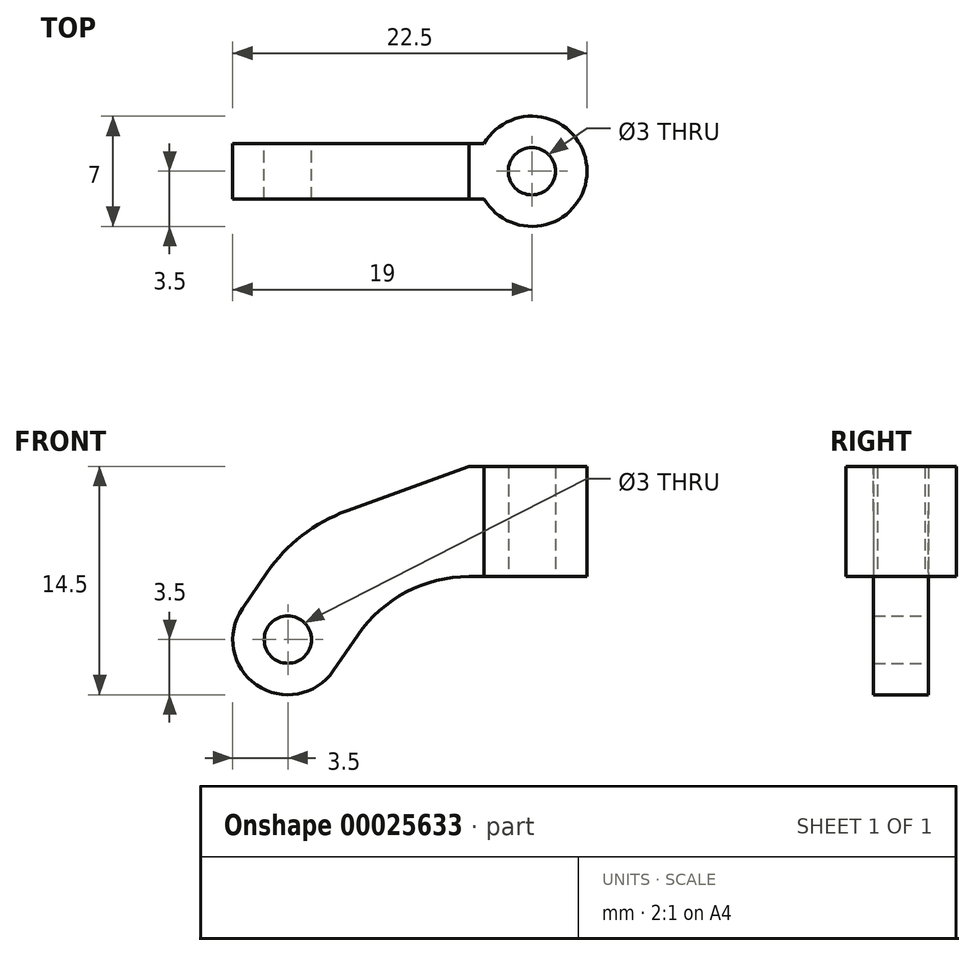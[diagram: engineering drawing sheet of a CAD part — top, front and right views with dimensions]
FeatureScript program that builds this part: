
annotation { "Feature Type Name" : "Feature", "Feature Type Description" : "" }
export const myFeature = defineFeature(function(context is Context, id is Id, definition is map)
    precondition{}
    {
        {
            var Q0;
            Q0=qCreatedBy(makeId("Top.planeOp"),FACE);
            var sketch = newSketch(context, id + "F0", { "sketchPlane" : qUnion([Q0])});
            skCircle(sketch, "E0", {"center": v(0, 0) * mm, "radius": 1.5 * mm});
            skCircle(sketch, "E1", {"center": v(0, 0) * mm, "radius": 3.5 * mm});
            skSolve(sketch);
        }
        {
            var Q0;
            Q0=makeQuery(id+"F0.imprint","IMPRINT",FACE,{"disambiguationData":[TD([[makeQuery(id+"F0.imprint","IMPRINT",EDGE,{"derivedFrom":sQuery(id+"F0.wireOp",EDGE,"E0")}),-1.0]])]});
            extrude(context, id + "F1", {"entities" : qUnion([Q0]), "depth" : 7 * mm});
        }
        {
            var Q0;
            Q0=qCreatedBy(makeId("Top.planeOp"),FACE);
            var sketch = newSketch(context, id + "F2", { "sketchPlane" : qUnion([Q0])});
            skLineSegment(sketch, "E2.bottom", {"start": v(0, 1.75) * mm, "end": v(-4, 1.75) * mm});
            skLineSegment(sketch, "E2.top", {"start": v(0, -1.75) * mm, "end": v(-4, -1.75) * mm});
            skLineSegment(sketch, "E2.left", {"start": v(0, 1.75) * mm, "end": v(0, 1.5) * mm});
            skLineSegment(sketch, "E2.right", {"start": v(-4, 1.75) * mm, "end": v(-4, -1.75) * mm});
            skArc(sketch, "E3.0", {"start": v(0, 1.5) * mm, "mid": v(-1.5, 0) * mm, "end": v(0, -1.5) * mm});
            skLineSegment(sketch, "E4.trimOffspring", {"start": v(0, -1.5) * mm, "end": v(0, -1.75) * mm});
            skLineSegment(sketch, "E5", {"start": v(0, 0) * mm, "end": v(-11, 0) * mm, "construction": true});
            skSolve(sketch);
        }
        {
            var Q0;
            Q0=makeQuery(id+"F2.imprint","IMPRINT",FACE,{"disambiguationData":[TD([[makeQuery(id+"F2.imprint","IMPRINT",EDGE,{"derivedFrom":sQuery(id+"F2.wireOp",EDGE,"E2.bottom")}),1.0]])]});
            extrude(context, id + "F3", {"entities" : qUnion([Q0]), "operationType" : NewBodyOperationType.ADD, "depth" : 7 * mm});
        }
        {
            var Q0;
            Q0=makeQuery(id+"F3.opExtrude","SWEPT_FACE",FACE,{"disambiguationData":[OSD([sQuery(id+"F2.wireOp",EDGE,"E2.bottom")])]});
            var sketch = newSketch(context, id + "F4", { "sketchPlane" : qUnion([Q0])});
            skArc(sketch, "E6", {"start": v(11.05, -3.7) * mm, "mid": v(7.98, -0.98) * mm, "end": v(4, 0) * mm});
            skCircle(sketch, "E7", {"center": v(15.5, -4) * mm, "radius": 1.5 * mm});
            skLineSegment(sketch, "E8", {"start": v(11.05, -3.7) * mm, "end": v(14.6, -8.87) * mm});
            skLineSegment(sketch, "E9", {"start": v(15.5, -4) * mm, "end": v(12.62, -5.98) * mm, "construction": true});
            skSolve(sketch);
        }
        {
            var Q0;
            Q0=makeQuery(id+"F3.opExtrude","SWEPT_FACE",FACE,{"disambiguationData":[OSD([sQuery(id+"F2.wireOp",EDGE,"E2.right")])]});
            var Q1;
            Q1=sQuery(id+"F4.wireOp",EDGE,"E6");
            var Q2;
            Q2=sQuery(id+"F4.wireOp",EDGE,"E8");
            sweep(context, id + "F5", {"operationType" : NewBodyOperationType.ADD, "profiles" : qUnion([Q0]), "path" : qUnion([Q1, Q2])});
        }
        {
            var Q0;
            Q0=sQuery(id+"F4.wireOp",VERTEX,"E7.center");
            var Q1;
            Q1=makeQuery(id+"F1.opExtrude","SWEPT_BODY",BODY,{"disambiguationData":[OSD([sQuery(id+"F0.wireOp",EDGE,"E0"),sQuery(id+"F0.wireOp",EDGE,"E1")])]});
            hole(context, id + "F6", {"style" : HoleStyle.SIMPLE, "holeDiameter" : 3 * mm, "endStyle" : HoleEndStyle.THROUGH, "locations" : qUnion([Q0]), "scope" : qUnion([Q1])});
        }
        {
            var Q0;
            {var subQ0=sQuery(id+"F2.wireOp",EDGE,"E2.right");var subQ1=sQuery(id+"F4.wireOp",VERTEX,"E8.end");Q0=makeQuery(id+"F5.opSweep","CAP_EDGE",EDGE,{"disambiguationData":[OSD([subQ0,subQ1]),TDD([makeQuery(id+"F3.opExtrude","CAP_EDGE",EDGE,{"disambiguationData":[OSD([subQ0])],"isStart":true}),subQ1])],"isStart":false});}
            var Q1;
            {var subQ0=sQuery(id+"F2.wireOp",EDGE,"E2.right");var subQ1=sQuery(id+"F4.wireOp",VERTEX,"E8.end");Q1=makeQuery(id+"F5.opSweep","CAP_EDGE",EDGE,{"disambiguationData":[OSD([subQ0,subQ1]),TDD([makeQuery(id+"F3.opExtrude","CAP_EDGE",EDGE,{"disambiguationData":[OSD([subQ0])],"isStart":false}),subQ1])],"isStart":false});}
            fillet(context, id + "F7", {"entities" : qUnion([Q0, Q1]), "radius" : 3.5 * mm, "tangentPropagation" : true, "allowEdgeOverflow" : false});
        }
        {
            var Q0;
            {var subQ0=sQuery(id+"F2.wireOp",EDGE,"E2.bottom");Q0=makeQuery(id+"F5.boolean.opBoolean","MERGE",FACE,{"derivedFrom":[makeQuery(id+"F3.opExtrude","SWEPT_FACE",FACE,{"disambiguationData":[OSD([subQ0])]}),makeQuery(id+"F5.opSweep","SWEPT_FACE",FACE,{"disambiguationData":[OSD([subQ0,sQuery(id+"F2.wireOp",EDGE,"E2.right"),sQuery(id+"F4.wireOp",EDGE,"E6")])]})]});}
            var sketch = newSketch(context, id + "F8", { "sketchPlane" : qUnion([Q0])});
            skLineSegment(sketch, "E10", {"start": v(4, 7) * mm, "end": v(9.18, 5.12) * mm});
            skLineSegment(sketch, "E11", {"start": v(24, -0.28) * mm, "end": v(24, 7) * mm});
            skLineSegment(sketch, "E12", {"start": v(24, 7) * mm, "end": v(4, 7) * mm});
            skArc(sketch, "E13.0", {"start": v(4, 7) * mm, "mid": v(11.24, 5.21) * mm, "end": v(16.82, 0.26) * mm});
            skLineSegment(sketch, "E14.trimOffspring", {"start": v(4, 7) * mm, "end": v(11.76, 4.18) * mm});
            skArc(sketch, "E15", {"start": v(16.82, 0.26) * mm, "mid": v(14.6, 2.61) * mm, "end": v(11.76, 4.18) * mm});
            skLineSegment(sketch, "E16.trimOffspring", {"start": v(14, 3.36) * mm, "end": v(24, -0.28) * mm});
            skLineSegment(sketch, "E17", {"start": v(11.76, 4.18) * mm, "end": v(9.18, 5.12) * mm});
            skSolve(sketch);
        }
        {
            var Q0;
            Q0 = qSketchRegion(id + "F8", true);
            extrude(context, id + "F9", {"entities" : qUnion([Q0]), "operationType" : NewBodyOperationType.REMOVE, "oppositeDirection" : true, "depth" : 25 * mm});
        }
    });
